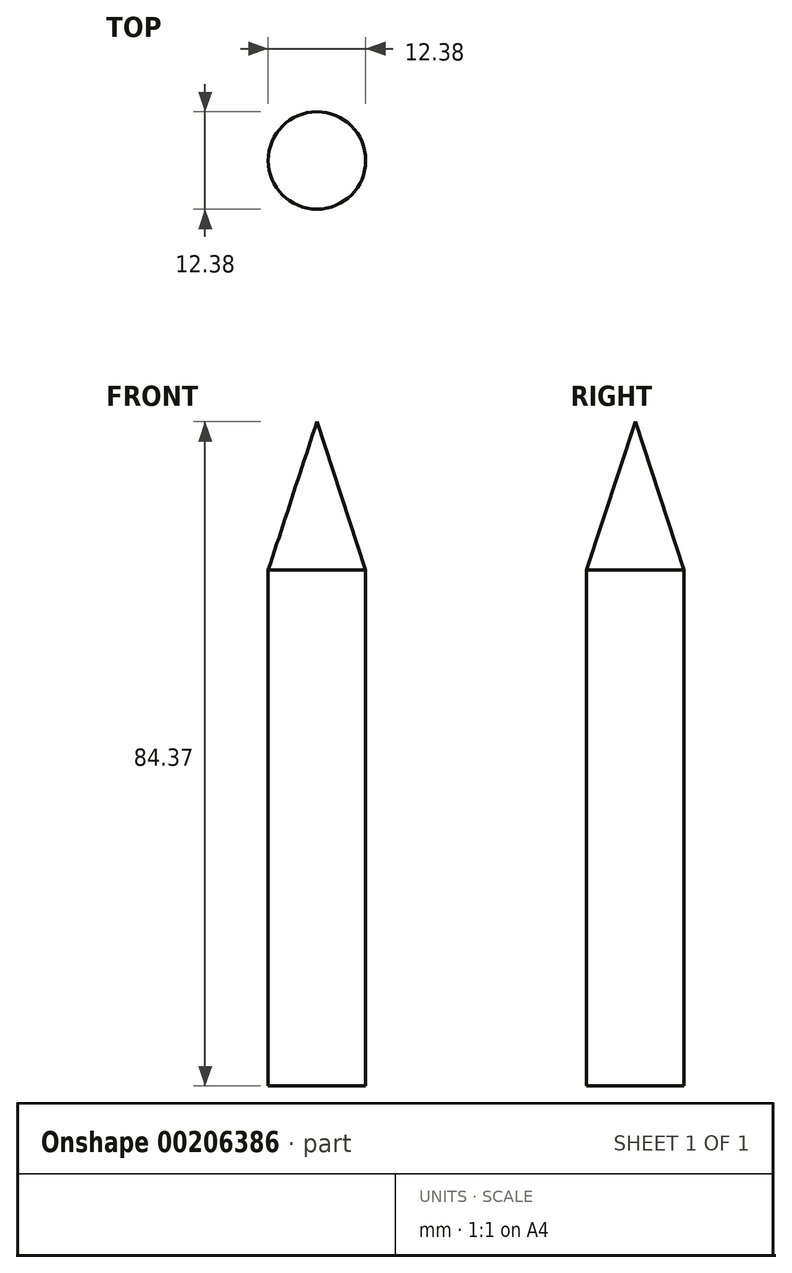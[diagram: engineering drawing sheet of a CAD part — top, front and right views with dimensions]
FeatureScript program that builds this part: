
annotation { "Feature Type Name" : "Feature", "Feature Type Description" : "" }
export const myFeature = defineFeature(function(context is Context, id is Id, definition is map)
    precondition{}
    {
        {
            var Q0;
            Q0=qCreatedBy(makeId("Front.planeOp"),FACE);
            var sketch = newSketch(context, id + "F0", { "sketchPlane" : qUnion([Q0])});
            skLineSegment(sketch, "E0", {"start": v(-12.19, 15.33) * mm, "end": v(-12.19, -50.2) * mm});
            skLineSegment(sketch, "E1", {"start": v(-12.19, -50.2) * mm, "end": v(-6, -50.2) * mm});
            skLineSegment(sketch, "E2", {"start": v(-6, -50.2) * mm, "end": v(-6, 34.17) * mm});
            skLineSegment(sketch, "E3", {"start": v(-6, 34.17) * mm, "end": v(-12.19, 15.33) * mm});
            skSolve(sketch);
        }
        {
            var Q0;
            Q0=makeQuery(id+"F0.imprint","IMPRINT",FACE,{"disambiguationData":[TD([[makeQuery(id+"F0.imprint","IMPRINT",EDGE,{"derivedFrom":sQuery(id+"F0.wireOp",EDGE,"E0")}),1.0]])]});
            var Q1;
            Q1=sQuery(id+"F0.wireOp",EDGE,"E2");
            revolve(context, id + "F1", {"entities" : qUnion([Q0]), "axis" : qUnion([Q1]), "revolveType" : RevolveType.FULL});
        }
    });
